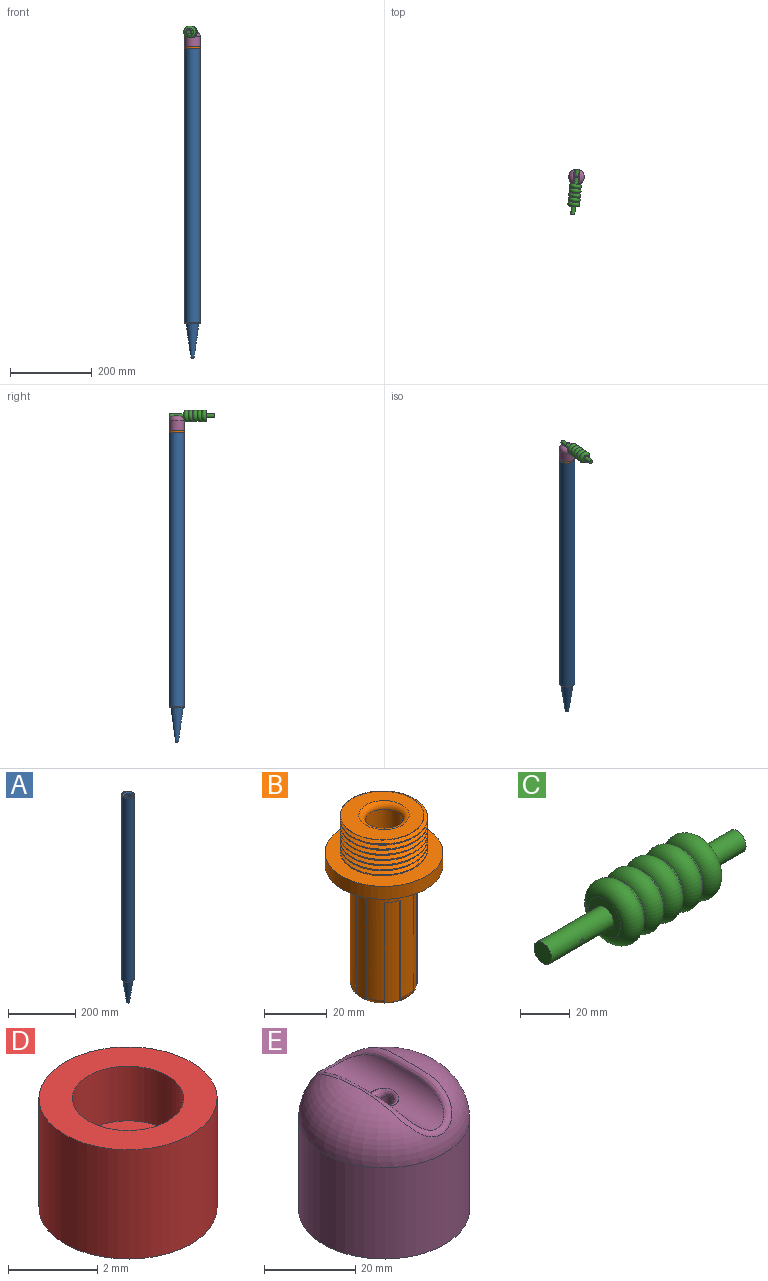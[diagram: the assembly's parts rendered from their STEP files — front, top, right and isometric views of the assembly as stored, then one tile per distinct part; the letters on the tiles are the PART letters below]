
ASSEMBLY  parts=5 mates=6
PART A: 10 faces, bbox 40.6x40.6x755 mm
  f0: plane 35.5x35.5mm, normal (0,0,-1), area 210.5mm2, adj f1,f9
  f1: cone r=15.75mm half-angle=7.9deg, axis (0,0,1), area 5279mm2, adj f0,f2
  f2: torus R=2.26mm, axis (0,0,1), area 62.4mm2, adj f1,f3
  f3: plane 4.52x4.52mm, normal (0,0,-1), area 16mm2, adj f2
  f4: plane 22x22mm, normal (0,0,1), area 380.1mm2, adj f5
  f5: cylinder r=11mm len=43mm, axis (0,0,1), area 2971.9mm2, adj f4,f6
  f6: torus R=16mm, axis (0,0,1), area 632.5mm2, adj f5,f7
  f7: plane 37.5x37.5mm, normal (0,0,1), area 300.2mm2, adj f6,f8
  f8: cylinder r=18.75mm len=669mm, axis (0,0,1), area 78814.7mm2, adj f7,f9
  f9: torus R=17.75mm, axis (0,0,1), area 181.5mm2, adj f0,f8
PART B: 40 faces, bbox 38.3x38.3x68.3 mm
  f0: cylinder r=10.75mm len=40mm, axis (0,0,1), area 1551.2mm2, adj f1,f14,f15,f16,f18,f19,f20,f22
  f1: torus R=8.75mm, axis (0,0,1), area 153.7mm2, adj f0,f9,f15,f16,f17,f19,f20,f21
  f2: cylinder r=6mm len=57.5mm, axis (0,0,-1), area 2167.7mm2, adj f12,f13
  f3: bspline ~32.04x27.75mm, area 839.3mm2, adj f5,f7,f10,f11
  f4: bspline ~32.04x27.75mm, area 833mm2, adj f5,f7,f10,f11
  f5: cylinder r=13.88mm len=27.75mm, axis (0,0,-1), area 252.6mm2, adj f3,f4,f7,f11
  f6: cylinder r=18.75mm len=37.5mm, axis (0,0,-1), area 589mm2, adj f7,f8
  f7: plane 38.25x38.25mm, normal (0,0,1), area 548.1mm2, adj f3,f4,f5,f6,f10
  f8: plane 37.5x37.5mm, normal (0,0,-1), area 325.2mm2, adj f6,f14
  f9: plane 17.5x17.5mm, normal (0,0,-1), area 237.4mm2, adj f1,f39
  f10: cylinder r=12.68mm len=25.35mm, axis (0,0,-1), area 44.2mm2, adj f3,f4,f7,f11
  f11: plane 27.47x27.37mm, normal (0,0,1), area 355.3mm2, adj f3,f4,f5,f10,f12
  f12: torus R=8mm, axis (0,0,1), area 132.8mm2, adj f2,f11
  f13: torus R=1mm, axis (0,0,-1), area 206.4mm2, adj f2,f39
  f14: torus R=15.75mm, axis (0,0,1), area 620.2mm2, adj f0,f8
  f15: plane 39.39x0.51mm, normal (-0.87,-0.5,0), area 20mm2, adj f0,f1,f17,f18
  f16: plane 39.39x0.51mm, normal (0.87,0.5,0), area 20mm2, adj f0,f1,f17,f18
  f17: cylinder r=10.25mm len=39.32mm, axis (0,0,-1), area 198.6mm2, adj f1,f15,f16,f18
  f18: plane 4.59x2.95mm, normal (0,0,-1), area 2.5mm2, adj f0,f15,f16,f17
  f19: plane 39.39x0.51mm, normal (-0.87,0.5,0), area 20mm2, adj f0,f1,f21,f22
  f20: plane 39.39x0.51mm, normal (0.87,-0.5,0), area 20mm2, adj f0,f1,f21,f22
  f21: cylinder r=10.25mm len=39.32mm, axis (0,0,-1), area 198.6mm2, adj f1,f19,f20,f22
  f22: plane 4.59x2.95mm, normal (0,0,-1), area 2.5mm2, adj f0,f19,f20,f21
  f23: plane 39.39x0.58mm, normal (0,1,0), area 20mm2, adj f0,f1,f25,f26
  f24: plane 39.39x0.58mm, normal (0,-1,0), area 20mm2, adj f0,f1,f25,f26
  f25: cylinder r=10.25mm len=39.32mm, axis (0,0,-1), area 198.6mm2, adj f1,f23,f24,f26
  f26: plane 5x0.81mm, normal (0,0,-1), area 2.5mm2, adj f0,f23,f24,f25
  f27: plane 39.39x0.51mm, normal (0.87,0.5,0), area 20mm2, adj f0,f1,f29,f30
  f28: plane 39.39x0.51mm, normal (-0.87,-0.5,0), area 20mm2, adj f0,f1,f29,f30
  f29: cylinder r=10.25mm len=39.32mm, axis (0,0,-1), area 198.6mm2, adj f1,f27,f28,f30
  f30: plane 4.59x2.95mm, normal (0,0,-1), area 2.5mm2, adj f0,f27,f28,f29
  f31: plane 39.39x0.51mm, normal (0.87,-0.5,0), area 20mm2, adj f0,f1,f33,f34
  f32: plane 39.39x0.51mm, normal (-0.87,0.5,0), area 20mm2, adj f0,f1,f33,f34
  f33: cylinder r=10.25mm len=39.32mm, axis (0,0,-1), area 198.6mm2, adj f1,f31,f32,f34
  f34: plane 4.59x2.95mm, normal (0,0,-1), area 2.5mm2, adj f0,f31,f32,f33
  f35: plane 39.39x0.58mm, normal (0,1,0), area 20mm2, adj f0,f1,f36,f38
  f36: cylinder r=10.25mm len=39.32mm, axis (0,0,-1), area 198.6mm2, adj f1,f35,f37,f38
  f37: plane 39.39x0.58mm, normal (0,-1,0), area 20mm2, adj f0,f1,f36,f38
  f38: plane 5x0.81mm, normal (0,0,-1), area 2.5mm2, adj f0,f35,f36,f37
  f39: cylinder r=1mm len=2mm, axis (0,0,-1), area 12.6mm2, adj f9,f13
PART C: 18 faces, bbox 110x31.4x31.4 mm
  f0: cylinder r=5mm len=35mm, axis (-1,0,0), area 1081.4mm2, adj f3,f4,f15,f17
  f1: torus R=11.4mm, axis (-1,0,0), area 80.2mm2, adj f2,f14
  f2: torus R=9mm, axis (-1,0,0), area 1213.5mm2, adj f1,f3
  f3: plane 18x18mm, normal (-1,0,0), area 175.9mm2, adj f0,f2
  f4: plane 10x10mm, normal (-1,0,0), area 78.5mm2, adj f0
  f5: plane 10x10mm, normal (1,0,0), area 78.5mm2, adj f6
  f6: cylinder r=5mm len=20mm, axis (-1,0,0), area 628.3mm2, adj f5,f7
  f7: plane 18x18mm, normal (1,0,0), area 175.9mm2, adj f6,f8
  f8: torus R=9mm, axis (-1,0,0), area 1213.5mm2, adj f7,f9
  f9: torus R=11.4mm, axis (-1,0,0), area 80.2mm2, adj f8,f10
  f10: torus R=9mm, axis (-1,0,0), area 1069.8mm2, adj f9,f11
  f11: torus R=11.4mm, axis (-1,0,0), area 80.2mm2, adj f10,f12
  f12: torus R=9mm, axis (-1,0,0), area 1069.8mm2, adj f11,f13
  f13: torus R=11.4mm, axis (-1,0,0), area 80.2mm2, adj f12,f14
  f14: torus R=9mm, axis (-1,0,0), area 1069.8mm2, adj f1,f13
  f15: cylinder r=2.25mm len=5mm, axis (0,-1,0), area 67mm2, adj f0,f16
  f16: plane 4.5x4.5mm, normal (0,1,0), area 14.1mm2, adj f15,f17
  f17: cylinder r=0.75mm len=5mm, axis (0,1,0), area 23.4mm2, adj f0,f16
PART D: 6 faces, bbox 4x4x3 mm
  f0: cylinder r=1.25mm len=2.5mm, axis (0,0,-1), area 11.8mm2, adj f2,f4
  f1: cylinder r=2mm len=4mm, axis (0,0,-1), area 37.7mm2, adj f2,f3
  f2: plane 4x4mm, normal (0,0,1), area 7.7mm2, adj f0,f1
  f3: plane 4x4mm, normal (0,0,-1), area 11.8mm2, adj f1,f5
  f4: plane 2.5x2.5mm, normal (0,0,1), area 4.1mm2, adj f0,f5
  f5: cylinder r=0.5mm len=1.5mm, axis (0,0,-1), area 4.7mm2, adj f3,f4
PART E: 16 faces, bbox 38.2x38.2x37.5 mm
  f0: plane 28.09x28.07mm, normal (0,0,-1), area 383mm2, adj f1,f11,f12,f13,f14
  f1: cylinder r=14.12mm len=28.25mm, axis (0,0,-1), area 477.7mm2, adj f0,f3,f12,f13
  f2: cylinder r=18.75mm len=37.5mm, axis (0,0,-1), area 2886.3mm2, adj f3,f4
  f3: plane 38.22x38.22mm, normal (0,0,-1), area 520.4mm2, adj f1,f2,f11,f12,f13
  f4: torus R=7.25mm, axis (0,0,1), area 1272mm2, adj f2,f9
  f5: cylinder r=6mm len=32.88mm, axis (0,-1,0), area 416.7mm2, adj f9,f10
  f6: cylinder r=6mm len=12mm, axis (0,0,-1), area 113.1mm2, adj f7,f14
  f7: sphere r=6mm, area 195.9mm2, adj f6,f15
  f8: cylinder r=2mm len=4mm, axis (0,0,1), area 29mm2, adj f10,f15
  f9: bspline ~35.53x15.11mm, area 183.5mm2, adj f4,f5
  f10: bspline ~7.01x5.61mm, area 30.4mm2, adj f5,f8
  f11: cylinder r=12.97mm len=25.95mm, axis (0,0,1), area 243mm2, adj f0,f3,f12,f13
  f12: bspline ~32.62x28.25mm, area 844.3mm2, adj f0,f1,f3,f11
  f13: bspline ~32.62x28.25mm, area 852.3mm2, adj f0,f1,f3,f11
  f14: torus R=8mm, axis (0,0,1), area 132.8mm2, adj f0,f6
  f15: torus R=4mm, axis (0,0,-1), area 30.9mm2, adj f7,f8
PLACE A t=(-28.89,-10.18,-374.25)mm fixed
PLACE B rot(axis=(0,0,1),116.1deg) t=(-28.89,-10.18,380.72)mm
PLACE C rot(axis=(0.54,-0.6,-0.6),123.4deg) t=(-38.2,-102.53,421.65)mm
PLACE D rot(axis=(0,0,1),40.6deg) t=(-28.89,-10.18,421.65)mm
PLACE E rot(axis=(0,0,1),174.2deg) t=(-28.89,-10.18,385.65)mm
MATE planar C.f15 <-> D.f1  axis (0,0,1) through (-28.89,-10.18,421.65)mm
MATE cylindrical C.f0 <-> E.f5  axis (0.1,0.99,0) through (-27.17,6.92,421.65)mm
MATE cylindrical C.f15 <-> A.f1  axis (0,0,-1) through (-28.89,-10.18,426.68)mm
MATE cylindrical E.f2 <-> B.f6  axis (0,0,-1) through (-28.89,-10.18,397.9)mm
MATE cylindrical B.f6 <-> A.f1  axis (0,0,-1) through (-28.89,-10.18,383.22)mm
MATE cylindrical D.f1 <-> C.f15  axis (0,0,-1) through (-28.89,-10.18,421.65)mm
